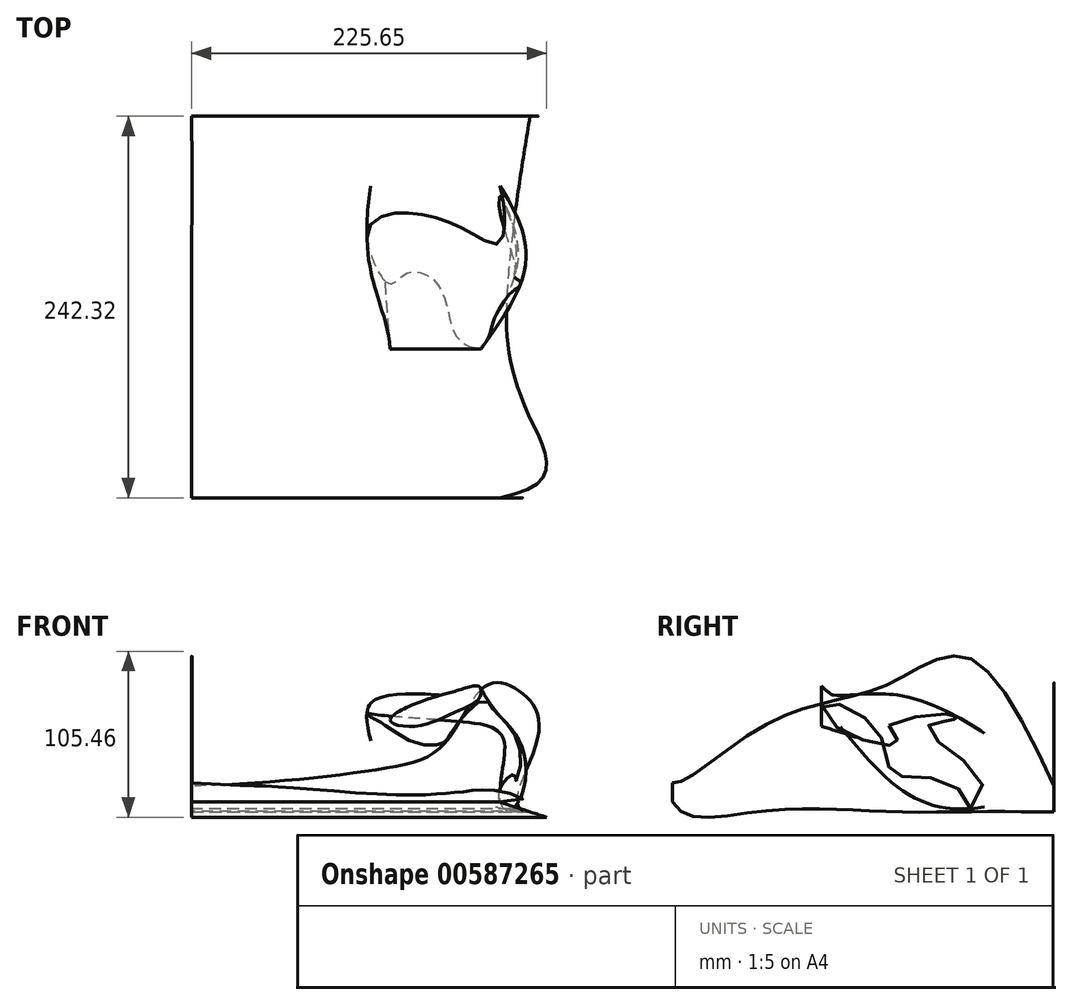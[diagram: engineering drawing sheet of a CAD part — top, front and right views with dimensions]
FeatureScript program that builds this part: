
annotation { "Feature Type Name" : "Feature", "Feature Type Description" : "" }
export const myFeature = defineFeature(function(context is Context, id is Id, definition is map)
    precondition{}
    {
        {
            var Q0;
            Q0=qCreatedBy(makeId("Front.planeOp"),FACE);
            var sketch = newSketch(context, id + "F0", { "sketchPlane" : qUnion([Q0])});
            skLineSegment(sketch, "E0", {"start": v(0, 0) * mm, "end": v(0, 16.55) * mm});
            skLineSegment(sketch, "E1", {"start": v(0, 0) * mm, "end": v(212.51, 0) * mm});
            skFitSpline(sketch, "E2", {"points": [v(212.51, 0) * mm, v(219.48, 45.29) * mm, v(209.3, 75.95) * mm, v(187.38, 80.63) * mm, v(161.75, 44.67) * mm, v(124.42, 28.04) * mm, v(0, 16.55) * mm], "startDerivative": vector(-338.48, 0) * mm, "endDerivative": vector(-515.1, -11.96) * mm});
            skSolve(sketch);
        }
        {
            var Q0;
            Q0=makeQuery(id+"F0.imprint","IMPRINT",FACE,{"disambiguationData":[TD([[makeQuery(id+"F0.imprint","IMPRINT",EDGE,{"derivedFrom":sQuery(id+"F0.wireOp",EDGE,"E0")}),-1.0]])]});
            cPlane(context, id + "F1", {"entities" : qUnion([Q0]), "cplaneType" : CPlaneType.OFFSET, "offset" : 100 * mm, "width" : 152.4 * mm, "height" : 152.4 * mm});
        }
        {
            var Q0;
            Q0=makeQuery(id+"F0.imprint","IMPRINT",FACE,{"disambiguationData":[TD([[makeQuery(id+"F0.imprint","IMPRINT",EDGE,{"derivedFrom":sQuery(id+"F0.wireOp",EDGE,"E0")}),-1.0]])]});
            cPlane(context, id + "F2", {"entities" : qUnion([Q0]), "cplaneType" : CPlaneType.OFFSET, "offset" : 200 * mm, "width" : 152.4 * mm, "height" : 152.4 * mm});
        }
        {
            var Q0;
            Q0=qCreatedBy(id+"F1.planeOp",FACE);
            var sketch = newSketch(context, id + "F3", { "sketchPlane" : qUnion([Q0])});
            skLineSegment(sketch, "E3", {"start": v(-16.14, 0) * mm, "end": v(-16.14, 16.5) * mm});
            skLineSegment(sketch, "E4", {"start": v(-16.14, 0) * mm, "end": v(198.67, 0) * mm});
            skFitSpline(sketch, "E5", {"points": [v(198.67, 0) * mm, v(203.32, 45.7) * mm, v(193.03, 75.84) * mm, v(171.26, 80.5) * mm, v(145.54, 44.65) * mm, v(108.27, 28.02) * mm, v(-16.14, 16.5) * mm], "startDerivative": vector(-338.6, 0) * mm, "endDerivative": vector(-515.1, -11.96) * mm});
            skSolve(sketch);
        }
        {
            var Q0;
            Q0=qCreatedBy(id+"F2.planeOp",FACE);
            var sketch = newSketch(context, id + "F4", { "sketchPlane" : qUnion([Q0])});
            skLineSegment(sketch, "E6", {"start": v(-16.15, -0.04) * mm, "end": v(-16.15, 83.62) * mm});
            skLineSegment(sketch, "E7", {"start": v(-16.15, -0.04) * mm, "end": v(184.86, -0.04) * mm});
            skFitSpline(sketch, "E8", {"points": [v(184.86, -0.04) * mm, v(188, 17.05) * mm, v(181.45, 51.58) * mm, v(152.65, 49.08) * mm, v(127.41, 43.28) * mm, v(72.6, 77.56) * mm, v(-16.15, 83.62) * mm], "startDerivative": vector(-338.6, 0) * mm, "endDerivative": vector(-570.4, 6.02) * mm});
            skSolve(sketch);
        }
        {
            var Q0;
            Q0=qCreatedBy(id+"F1.planeOp",FACE);
            cPlane(context, id + "F5", {"entities" : qUnion([Q0]), "cplaneType" : CPlaneType.OFFSET, "offset" : 189.48 * mm, "width" : 152.4 * mm, "height" : 152.4 * mm});
        }
        {
            var Q0;
            Q0=qCreatedBy(id+"F1.planeOp",FACE);
            cPlane(context, id + "F6", {"entities" : qUnion([Q0]), "cplaneType" : CPlaneType.OFFSET, "offset" : 51.82 * mm, "width" : 152.4 * mm, "height" : 152.4 * mm});
        }
        {
            var Q0;
            Q0=qCreatedBy(id+"F1.planeOp",FACE);
            cPlane(context, id + "F7", {"entities" : qUnion([Q0]), "cplaneType" : CPlaneType.OFFSET, "offset" : 147.83 * mm, "width" : 152.4 * mm, "height" : 152.4 * mm});
        }
        {
            var Q0;
            Q0=qCreatedBy(id+"F7.planeOp",FACE);
            cPlane(context, id + "F8", {"entities" : qUnion([Q0]), "cplaneType" : CPlaneType.OFFSET, "offset" : 88.65 * mm, "width" : 152.4 * mm, "height" : 152.4 * mm});
        }
        {
            var Q0;
            Q0=qCreatedBy(id+"F8.planeOp",FACE);
            var sketch = newSketch(context, id + "F9", { "sketchPlane" : qUnion([Q0])});
            skLineSegment(sketch, "E9", {"start": v(-16.4, 0) * mm, "end": v(-16.4, 19.52) * mm});
            skLineSegment(sketch, "E10", {"start": v(-16.4, 0) * mm, "end": v(198.56, 0) * mm});
            skFitSpline(sketch, "E11", {"points": [v(198.56, 0) * mm, v(192.76, 17.85) * mm, v(175.72, 30.05) * mm, v(153.55, 27.06) * mm, v(139.43, 20.45) * mm, v(103.37, 13.14) * mm, v(-16.4, 19.52) * mm], "startDerivative": vector(-338.8, 0) * mm, "endDerivative": vector(-515.1, -11.96) * mm});
            skSolve(sketch);
        }
        {
            var Q0;
            Q0=qCreatedBy(id+"F6.planeOp",FACE);
            var sketch = newSketch(context, id + "F10", { "sketchPlane" : qUnion([Q0])});
            skLineSegment(sketch, "E12", {"start": v(-16.13, 0.13) * mm, "end": v(-16.13, 96.65) * mm});
            skLineSegment(sketch, "E13", {"start": v(-16.13, 0.13) * mm, "end": v(190.53, 0.13) * mm});
            skFitSpline(sketch, "E14", {"points": [v(190.53, 0.13) * mm, v(180.21, 21.19) * mm, v(176.47, 60.79) * mm, v(104.5, 65.81) * mm, v(26.5, 99.26) * mm, v(-5.92, 97.22) * mm, v(-16.13, 96.65) * mm], "startDerivative": vector(-338.72, 0) * mm, "endDerivative": vector(-375.3, 0) * mm});
            skSolve(sketch);
        }
        {
            var Q0;
            Q0=qCreatedBy(id+"F5.planeOp",FACE);
            var sketch = newSketch(context, id + "F11", { "sketchPlane" : qUnion([Q0])});
            skLineSegment(sketch, "E15", {"start": v(-16.26, -0.04) * mm, "end": v(-16.26, 51.77) * mm});
            skLineSegment(sketch, "E16", {"start": v(-16.26, -0.04) * mm, "end": v(197.65, -0.04) * mm});
            skFitSpline(sketch, "E17", {"points": [v(197.65, -0.04) * mm, v(204.55, 45.23) * mm, v(194.37, 75.9) * mm, v(171.38, 75.32) * mm, v(138.62, 47.14) * mm, v(88.16, 47.72) * mm, v(-16.26, 51.77) * mm], "startDerivative": vector(-338.47, 0) * mm, "endDerivative": vector(-515.1, -11.96) * mm});
            skSolve(sketch);
        }
        {
            var Q0;
            Q0=qCreatedBy(makeId("Right.planeOp"),FACE);
            cPlane(context, id + "F12", {"entities" : qUnion([Q0]), "cplaneType" : CPlaneType.OFFSET, "offset" : 198.73 * mm, "width" : 152.4 * mm, "height" : 152.4 * mm});
        }
        {
            var Q0;
            Q0=qCreatedBy(makeId("Right.planeOp"),FACE);
            cPlane(context, id + "F13", {"entities" : qUnion([Q0]), "cplaneType" : CPlaneType.OFFSET, "offset" : 16.26 * mm, "oppositeDirection" : true, "width" : 152.4 * mm, "height" : 152.4 * mm});
        }
        {
            var Q0;
            Q0=qCreatedBy(id+"F8.planeOp",FACE);
            cPlane(context, id + "F14", {"entities" : qUnion([Q0]), "cplaneType" : CPlaneType.OFFSET, "offset" : 5.84 * mm, "width" : 152.4 * mm, "height" : 152.4 * mm});
        }
        {
            var Q0;
            Q0=qCreatedBy(id+"F14.planeOp",FACE);
            var sketch = newSketch(context, id + "F15", { "sketchPlane" : qUnion([Q0])});
            skLineSegment(sketch, "E18", {"start": v(-16.44, 6.21) * mm, "end": v(-16.44, 18.37) * mm});
            skLineSegment(sketch, "E19", {"start": v(-16.44, 6.21) * mm, "end": v(179.4, 6.21) * mm});
            skFitSpline(sketch, "E20", {"points": [v(179.4, 6.21) * mm, v(185.88, 11.8) * mm, v(158.54, 13.1) * mm, v(144.2, 11.73) * mm, v(114.25, 10.73) * mm, v(39.79, 15.91) * mm, v(-16.44, 18.37) * mm], "startDerivative": vector(789.12, 0) * mm, "endDerivative": vector(-506.1, 30.3) * mm});
            skSolve(sketch);
        }
        {
            var Q0;
            Q0=qCreatedBy(id+"F7.planeOp",FACE);
            var sketch = newSketch(context, id + "F16", { "sketchPlane" : qUnion([Q0])});
            skFitSpline(sketch, "E21", {"points": [v(109.85, 58.47) * mm, v(131.3, 70.81) * mm, v(152, 76.93) * mm, v(166.45, 79.49) * mm, v(166.59, 72.65) * mm, v(153.91, 64.61) * mm, v(125.1, 54.38) * mm, v(109.85, 58.47) * mm]});
            skSolve(sketch);
        }
        {
            var Q0;
            Q0=qCreatedBy(id+"F2.planeOp",FACE);
            var sketch = newSketch(context, id + "F17", { "sketchPlane" : qUnion([Q0])});
            skFitSpline(sketch, "E22", {"points": [v(118.5, 46.92) * mm, v(99.58, 70.57) * mm, v(186.48, 52.09) * mm, v(191.82, 19.58) * mm, v(188.91, 16.3) * mm, v(189.32, 20.35) * mm, v(181.81, 32.6) * mm, v(118.5, 46.92) * mm]});
            skSolve(sketch);
        }
        {
            var Q0;
            Q0=qCreatedBy(id+"F1.planeOp",FACE);
            var sketch = newSketch(context, id + "F18", { "sketchPlane" : qUnion([Q0])});
            skFitSpline(sketch, "E23", {"points": [v(107.59, 16.85) * mm, v(115.36, 16.55) * mm, v(123.56, 22.88) * mm, v(143.9, 25.17) * mm, v(147.68, 18.53) * mm, v(97.54, 7.04) * mm, v(98.95, 19.05) * mm, v(107.59, 16.85) * mm]});
            skSolve(sketch);
        }
        {
            var Q0;
            Q0=makeQuery(id+"F3.imprint","IMPRINT",FACE,{"disambiguationData":[TD([[makeQuery(id+"F3.imprint","IMPRINT",EDGE,{"derivedFrom":sQuery(id+"F3.wireOp",EDGE,"E3")}),-1.0]])]});
            var Q1;
            Q1=makeQuery(id+"F10.imprint","IMPRINT",FACE,{"disambiguationData":[TD([[makeQuery(id+"F10.imprint","IMPRINT",EDGE,{"derivedFrom":sQuery(id+"F10.wireOp",EDGE,"E12")}),-1.0]])]});
            var Q2;
            Q2=makeQuery(id+"F4.imprint","IMPRINT",FACE,{"disambiguationData":[TD([[makeQuery(id+"F4.imprint","IMPRINT",EDGE,{"derivedFrom":sQuery(id+"F4.wireOp",EDGE,"E6")}),-1.0]])]});
            var Q3;
            Q3=makeQuery(id+"F11.imprint","IMPRINT",FACE,{"disambiguationData":[TD([[makeQuery(id+"F11.imprint","IMPRINT",EDGE,{"derivedFrom":sQuery(id+"F11.wireOp",EDGE,"E15")}),-1.0]])]});
            var Q4;
            Q4=makeQuery(id+"F9.imprint","IMPRINT",FACE,{"disambiguationData":[TD([[makeQuery(id+"F9.imprint","IMPRINT",EDGE,{"derivedFrom":sQuery(id+"F9.wireOp",EDGE,"E9")}),-1.0]])]});
            var Q5;
            Q5=makeQuery(id+"F15.imprint","IMPRINT",FACE,{"disambiguationData":[TD([[makeQuery(id+"F15.imprint","IMPRINT",EDGE,{"derivedFrom":sQuery(id+"F15.wireOp",EDGE,"E18")}),-1.0]])]});
            loft(context, id + "F19", {"sheetProfilesArray" : [{ "sheetProfileEntities" : qUnion([Q0]) }, { "sheetProfileEntities" : qUnion([Q1]) }, { "sheetProfileEntities" : qUnion([Q2]) }, { "sheetProfileEntities" : qUnion([Q3]) }, { "sheetProfileEntities" : qUnion([Q4]) }, { "sheetProfileEntities" : qUnion([Q5]) }]});
        }
        {
            var Q1;
            Q1=makeQuery(id+"F16.imprint","IMPRINT",FACE,{"disambiguationData":[TD([[makeQuery(id+"F16.imprint","IMPRINT",EDGE,{"derivedFrom":sQuery(id+"F16.wireOp",EDGE,"E21")}),-1.0]])]});
            var Q2;
            Q2=makeQuery(id+"F17.imprint","IMPRINT",FACE,{"disambiguationData":[TD([[makeQuery(id+"F17.imprint","IMPRINT",EDGE,{"derivedFrom":sQuery(id+"F17.wireOp",EDGE,"E22")}),-1.0]])]});
            var Q3;
            Q3=makeQuery(id+"F18.imprint","IMPRINT",FACE,{"disambiguationData":[TD([[makeQuery(id+"F18.imprint","IMPRINT",EDGE,{"derivedFrom":sQuery(id+"F18.wireOp",EDGE,"E23")}),-1.0]])]});
            loft(context, id + "F20", {"operationType" : NewBodyOperationType.ADD, "sheetProfilesArray" : [{ "sheetProfileEntities" : qUnion([Q1]) }, { "sheetProfileEntities" : qUnion([Q2]) }, { "sheetProfileEntities" : qUnion([Q3]) }]});
        }
    });
